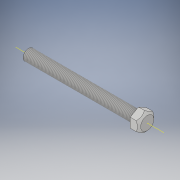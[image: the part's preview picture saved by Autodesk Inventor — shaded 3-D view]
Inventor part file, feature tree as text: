
AUTODESK INVENTOR PART (.ipt)
format: ipt  version: 2018 (Build 220112000, 112)  size: 122,880 bytes
history: native  units: in
note: dims shown in document units (in); Inventor stores cm internally (conversion verified against a paired STEP export)
features: sketch x3, revolve x2, extrude x1, other x1, thread x1
ambient origin geometry x8: Origin, YZ Plane, XZ Plane, XY Plane, X Axis, Y Axis, Z Axis, Center Point
bodies: Solid1 (feature_tree)
feature tree (8):
  revolve  "Revolution1"  [1 undecoded]
  extrude  "Extrusion1"  Depth=0.5906in
  sketch  "Sketch3"  dims[d4=0.6299in d5=0.0in d6=90.0deg d7=0.3937in d8=0.0in]
  other  "Work Axis1"
  revolve  "Revolution2"  Angle=90.0deg
  thread  "Thread1"  [1 undecoded]
  sketch  "Sketch1"  dims[d0=0.3937in d1=7.874in]
  sketch  "Sketch2"  dims[d2=90.0deg d3=0.5906in]
note: 2 required parameter values undecoded (feature->parameter linkage not recoverable at this tier; creation-order binding heuristic only, values carry confidence <= 0.55)